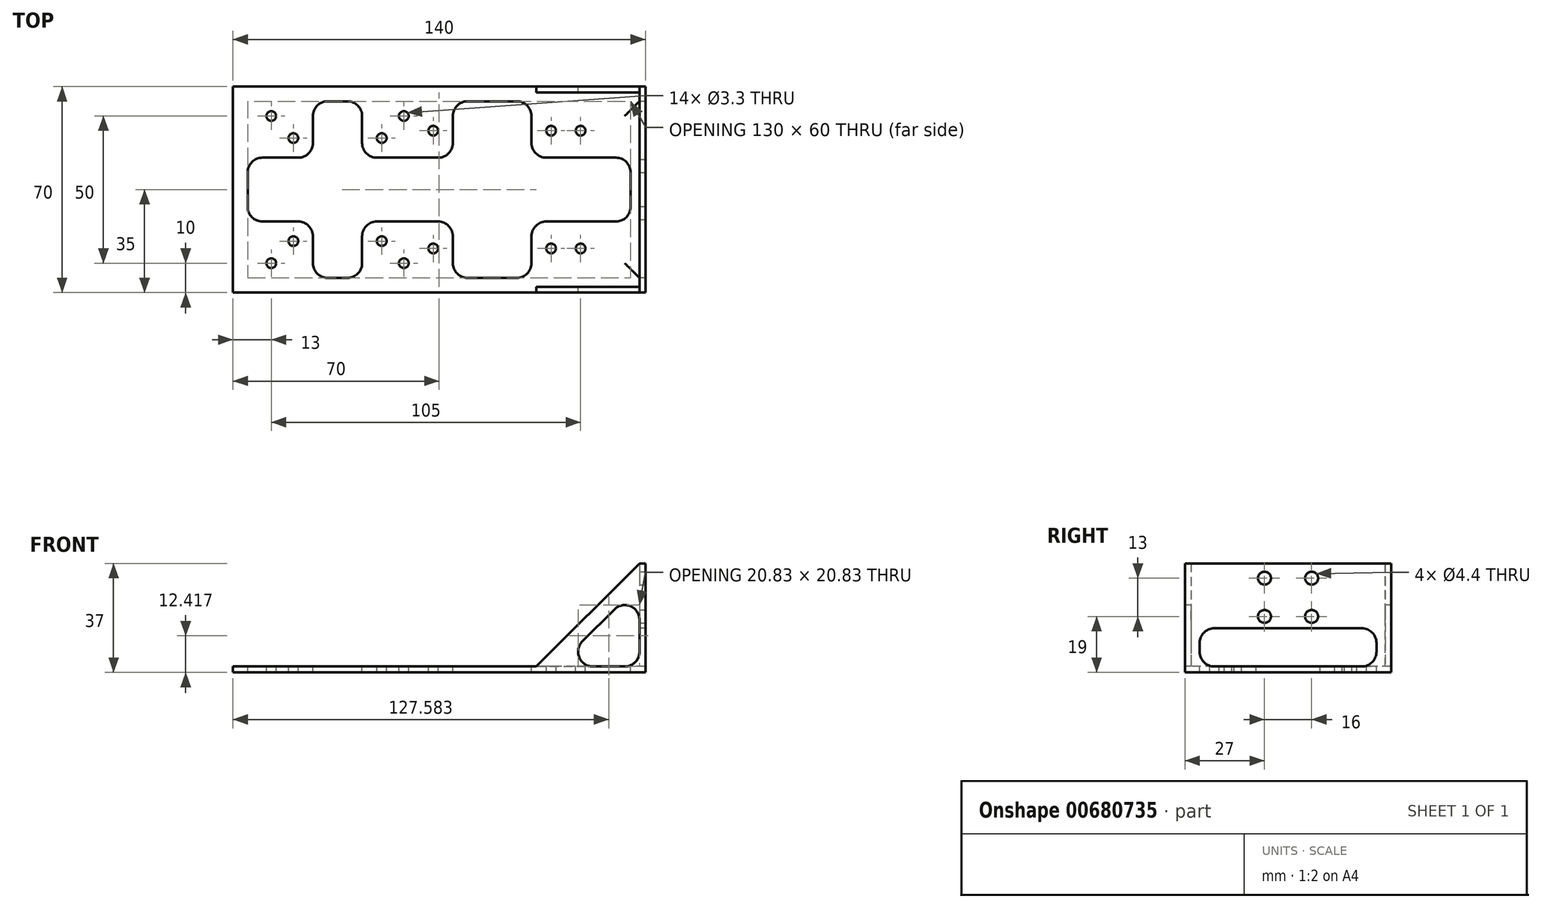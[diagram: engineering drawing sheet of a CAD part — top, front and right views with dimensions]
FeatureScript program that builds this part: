
annotation { "Feature Type Name" : "Feature", "Feature Type Description" : "" }
export const myFeature = defineFeature(function(context is Context, id is Id, definition is map)
    precondition{}
    {
        {
            var Q0;
            Q0=qCreatedBy(makeId("Top.planeOp"),FACE);
            var sketch = newSketch(context, id + "F0", { "sketchPlane" : qUnion([Q0])});
            skLineSegment(sketch, "E0.bottom", {"start": v(-80, 35) * mm, "end": v(60, 35) * mm});
            skLineSegment(sketch, "E0.top", {"start": v(-80, -35) * mm, "end": v(60, -35) * mm});
            skLineSegment(sketch, "E0.left", {"start": v(-80, 35) * mm, "end": v(-80, -35) * mm});
            skLineSegment(sketch, "E0.right", {"start": v(60, 35) * mm, "end": v(60, -35) * mm});
            skSolve(sketch);
        }
        {
            var Q0;
            Q0 = qSketchRegion(id + "F0", true);
            extrude(context, id + "F1", {"entities" : qUnion([Q0]), "depth" : 37 * mm, "offsetDistance" : 25 * mm});
        }
        {
            var Q0;
            Q0=makeQuery(id+"F1.opExtrude","SWEPT_FACE",FACE,{"disambiguationData":[OSD([sQuery(id+"F0.wireOp",EDGE,"E0.top")])]});
            var sketch = newSketch(context, id + "F2", { "sketchPlane" : qUnion([Q0])});
            skLineSegment(sketch, "E1.bottom", {"start": v(-80, 37) * mm, "end": v(58, 37) * mm});
            skLineSegment(sketch, "E1.top", {"start": v(-80, 2) * mm, "end": v(58, 2) * mm});
            skLineSegment(sketch, "E1.left", {"start": v(-80, 37) * mm, "end": v(-80, 2) * mm});
            skLineSegment(sketch, "E2", {"start": v(58, 37) * mm, "end": v(58, 2) * mm});
            skSolve(sketch);
        }
        {
            var Q0;
            Q0=makeQuery(id+"F2.imprint","IMPRINT",FACE,{"disambiguationData":[TD([[makeQuery(id+"F2.imprint","IMPRINT",EDGE,{"derivedFrom":sQuery(id+"F2.wireOp",EDGE,"E1.bottom")}),-1.0]])]});
            var Q1;
            Q1=makeQuery(id+"F2.imprint","IMPRINT",FACE,{"disambiguationData":[TD([[makeQuery(id+"F2.imprint","IMPRINT",EDGE,{"derivedFrom":sQuery(id+"F2.wireOp",EDGE,"E1.right")}),1.0]])]});
            extrude(context, id + "F3", {"entities" : qUnion([Q0, Q1]), "operationType" : NewBodyOperationType.REMOVE, "endBound" : BoundingType.THROUGH_ALL, "oppositeDirection" : true, "depth" : 25 * mm, "offsetDistance" : 25 * mm});
        }
        {
            var Q0;
            Q0=makeQuery(id+"F3.boolean.opBoolean","COPY",FACE,{"derivedFrom":makeQuery(id+"F3.opExtrude","SWEPT_FACE",FACE,{"disambiguationData":[OSD([sQuery(id+"F2.wireOp",EDGE,"E1.top")])]})});
            var sketch = newSketch(context, id + "F4", { "sketchPlane" : qUnion([Q0])});
            skPoint(sketch, "E3", {"position": v(38, -20) * mm});
            skPoint(sketch, "E4", {"position": v(38, 20) * mm});
            skPoint(sketch, "E5", {"position": v(28, 20) * mm});
            skPoint(sketch, "E6", {"position": v(28, -20) * mm});
            skPoint(sketch, "E7", {"position": v(-12, -20) * mm});
            skPoint(sketch, "E8", {"position": v(-12, 20) * mm});
            skPoint(sketch, "E9", {"position": v(-67, 25) * mm});
            skPoint(sketch, "E10", {"position": v(-59.5, -17.5) * mm});
            skPoint(sketch, "E11", {"position": v(-29.5, 17.5) * mm});
            skPoint(sketch, "E12", {"position": v(-29.5, -17.5) * mm});
            skPoint(sketch, "E13", {"position": v(-22, 25) * mm});
            skPoint(sketch, "E14", {"position": v(-67, -25) * mm});
            skPoint(sketch, "E15", {"position": v(-22, -25) * mm});
            skPoint(sketch, "E16", {"position": v(-59.5, 17.5) * mm});
            skSolve(sketch);
        }
        {
            var Q0;
            Q0=sQuery(id+"F4.wireOp",VERTEX,"E9");
            var Q1;
            Q1=sQuery(id+"F4.wireOp",VERTEX,"E16");
            var Q2;
            Q2=sQuery(id+"F4.wireOp",VERTEX,"E14");
            var Q3;
            Q3=sQuery(id+"F4.wireOp",VERTEX,"E10");
            var Q4;
            Q4=sQuery(id+"F4.wireOp",VERTEX,"E12");
            var Q5;
            Q5=sQuery(id+"F4.wireOp",VERTEX,"E15");
            var Q6;
            Q6=sQuery(id+"F4.wireOp",VERTEX,"E7");
            var Q7;
            Q7=sQuery(id+"F4.wireOp",VERTEX,"E8");
            var Q8;
            Q8=sQuery(id+"F4.wireOp",VERTEX,"E13");
            var Q9;
            Q9=sQuery(id+"F4.wireOp",VERTEX,"E11");
            var Q10;
            Q10=sQuery(id+"F4.wireOp",VERTEX,"E5");
            var Q11;
            Q11=sQuery(id+"F4.wireOp",VERTEX,"E4");
            var Q12;
            Q12=sQuery(id+"F4.wireOp",VERTEX,"E3");
            var Q13;
            Q13=sQuery(id+"F4.wireOp",VERTEX,"E6");
            var Q14;
            Q14=makeQuery(id+"F1.opExtrude","SWEPT_BODY",BODY,{"disambiguationData":[OSD([sQuery(id+"F0.wireOp",EDGE,"E0.bottom"),sQuery(id+"F0.wireOp",EDGE,"E0.top"),sQuery(id+"F0.wireOp",EDGE,"E0.left"),sQuery(id+"F0.wireOp",EDGE,"E0.right")])]});
            hole(context, id + "F5", {"style" : HoleStyle.SIMPLE, "endStyle" : HoleEndStyle.THROUGH, "standardTappedOrClearance" : lookupTablePath({ "standard" : "ISO", "fit" : "Normal", "size" : "M3", "type" : "Clearance" }), "standardBlindInLast" : lookupTablePath({ "fit" : "Standard", "standard" : "ISO", "size" : "M3", "type" : "Clearance" }), "holeDiameter" : 3.3 * mm, "majorDiameter" : 5 * mm, "isTappedThrough" : true, "tappedDepth" : 12 * mm, "tapClearance" : 3, "locations" : qUnion([Q0, Q1, Q2, Q3, Q4, Q5, Q6, Q7, Q8, Q9, Q10, Q11, Q12, Q13]), "scope" : qUnion([Q14])});
        }
        {
            var Q0;
            Q0=makeQuery(id+"F3.boolean.opBoolean","COPY",FACE,{"derivedFrom":makeQuery(id+"F3.opExtrude","SWEPT_FACE",FACE,{"disambiguationData":[OSD([sQuery(id+"F2.wireOp",EDGE,"E2")])]})});
            var sketch = newSketch(context, id + "F6", { "sketchPlane" : qUnion([Q0])});
            skLineSegment(sketch, "E17.bottom", {"start": v(-35, 37) * mm, "end": v(-33, 37) * mm});
            skLineSegment(sketch, "E17.top", {"start": v(-35, 2) * mm, "end": v(-33, 2) * mm});
            skLineSegment(sketch, "E17.left", {"start": v(-35, 37) * mm, "end": v(-35, 2) * mm});
            skLineSegment(sketch, "E17.right", {"start": v(-33, 37) * mm, "end": v(-33, 2) * mm});
            skLineSegment(sketch, "E18.bottom", {"start": v(35, 37) * mm, "end": v(33, 37) * mm});
            skLineSegment(sketch, "E18.top", {"start": v(35, 2) * mm, "end": v(33, 2) * mm});
            skLineSegment(sketch, "E18.left", {"start": v(35, 37) * mm, "end": v(35, 2) * mm});
            skLineSegment(sketch, "E18.right", {"start": v(33, 37) * mm, "end": v(33, 2) * mm});
            skSolve(sketch);
        }
        {
            var Q0;
            Q0 = qSketchRegion(id + "F6", true);
            extrude(context, id + "F7", {"entities" : qUnion([Q0]), "operationType" : NewBodyOperationType.ADD, "depth" : 35 * mm, "offsetDistance" : 25 * mm});
        }
        {
            var Q0;
            Q0=makeQuery(id+"F7.opExtrude","CAP_EDGE",EDGE,{"disambiguationData":[OSD([sQuery(id+"F6.wireOp",EDGE,"E18.bottom")])],"isStart":false});
            var Q1;
            Q1=makeQuery(id+"F7.opExtrude","CAP_EDGE",EDGE,{"disambiguationData":[OSD([sQuery(id+"F6.wireOp",EDGE,"E17.bottom")])],"isStart":false});
            chamfer(context, id + "F8", {"entities" : qUnion([Q0, Q1]), "width" : 35 * mm, "tangentPropagation" : true});
        }
        {
            var Q0;
            Q0=makeQuery(id+"F7.boolean.opBoolean","MERGE",FACE,{"derivedFrom":[makeQuery(id+"F1.opExtrude","SWEPT_FACE",FACE,{"disambiguationData":[OSD([sQuery(id+"F0.wireOp",EDGE,"E0.top")])]}),makeQuery(id+"F7.opExtrude","SWEPT_FACE",FACE,{"disambiguationData":[OSD([sQuery(id+"F6.wireOp",EDGE,"E18.left")])]})]});
            var sketch = newSketch(context, id + "F9", { "sketchPlane" : qUnion([Q0])});
            skLineSegment(sketch, "E19", {"start": v(58, 29.93) * mm, "end": v(30.07, 2) * mm});
            skLineSegment(sketch, "E20", {"start": v(30.07, 2) * mm, "end": v(58, 2) * mm});
            skLineSegment(sketch, "E21", {"start": v(58, 2) * mm, "end": v(58, 29.93) * mm});
            skSolve(sketch);
        }
        {
            var Q0;
            Q0 = qSketchRegion(id + "F9", true);
            extrude(context, id + "F10", {"entities" : qUnion([Q0]), "operationType" : NewBodyOperationType.REMOVE, "endBound" : BoundingType.THROUGH_ALL, "oppositeDirection" : true, "depth" : 25 * mm, "offsetDistance" : 25 * mm});
        }
        {
            var Q0;
            Q0=makeQuery(id+"F10.boolean.opBoolean","MERGE",FACE,{"derivedFrom":[makeQuery(id+"F3.boolean.opBoolean","COPY",FACE,{"derivedFrom":makeQuery(id+"F3.opExtrude","SWEPT_FACE",FACE,{"disambiguationData":[OSD([sQuery(id+"F2.wireOp",EDGE,"E2")])]})}),makeQuery(id+"F10.opExtrude","SWEPT_FACE",FACE,{"disambiguationData":[OSD([sQuery(id+"F9.wireOp",EDGE,"E21")])]})]});
            var sketch = newSketch(context, id + "F11", { "sketchPlane" : qUnion([Q0])});
            skLineSegment(sketch, "E22.bottom", {"start": v(-30, 15) * mm, "end": v(30, 15) * mm});
            skLineSegment(sketch, "E22.top", {"start": v(-30, 2) * mm, "end": v(30, 2) * mm});
            skLineSegment(sketch, "E22.left", {"start": v(-30, 15) * mm, "end": v(-30, 2) * mm});
            skLineSegment(sketch, "E22.right", {"start": v(30, 15) * mm, "end": v(30, 2) * mm});
            skSolve(sketch);
        }
        {
            var Q0;
            Q0 = qSketchRegion(id + "F11", true);
            extrude(context, id + "F12", {"entities" : qUnion([Q0]), "operationType" : NewBodyOperationType.REMOVE, "endBound" : BoundingType.THROUGH_ALL, "oppositeDirection" : true, "depth" : 25 * mm, "offsetDistance" : 25 * mm});
        }
        {
            var Q0;
            Q0=makeQuery(id+"F12.boolean.opBoolean","MERGE",FACE,{"derivedFrom":[makeQuery(id+"F10.boolean.opBoolean","MERGE",FACE,{"derivedFrom":[makeQuery(id+"F3.boolean.opBoolean","COPY",FACE,{"derivedFrom":makeQuery(id+"F3.opExtrude","SWEPT_FACE",FACE,{"disambiguationData":[OSD([sQuery(id+"F2.wireOp",EDGE,"E1.top")])]})}),makeQuery(id+"F10.opExtrude","SWEPT_FACE",FACE,{"disambiguationData":[OSD([sQuery(id+"F9.wireOp",EDGE,"E20")])]})]}),makeQuery(id+"F12.opExtrude","SWEPT_FACE",FACE,{"disambiguationData":[OSD([sQuery(id+"F11.wireOp",EDGE,"E22.top")])]})]});
            var sketch = newSketch(context, id + "F13", { "sketchPlane" : qUnion([Q0])});
            skLineSegment(sketch, "E23.bottom", {"start": v(55, 10.85) * mm, "end": v(-75, 10.85) * mm});
            skLineSegment(sketch, "E23.top", {"start": v(55, -10.85) * mm, "end": v(-75, -10.85) * mm});
            skLineSegment(sketch, "E23.left", {"start": v(55, 10.85) * mm, "end": v(55, -10.85) * mm});
            skLineSegment(sketch, "E23.right", {"start": v(-75, 10.85) * mm, "end": v(-75, -10.85) * mm});
            skLineSegment(sketch, "E24.bottom", {"start": v(21.35, 30) * mm, "end": v(-5.35, 30) * mm});
            skLineSegment(sketch, "E24.top", {"start": v(21.35, -30) * mm, "end": v(-5.35, -30) * mm});
            skLineSegment(sketch, "E24.left", {"start": v(21.35, 30) * mm, "end": v(21.35, -30) * mm});
            skLineSegment(sketch, "E24.right", {"start": v(-5.35, 30) * mm, "end": v(-5.35, -30) * mm});
            skLineSegment(sketch, "E25.bottom", {"start": v(-36.15, 30) * mm, "end": v(-52.85, 30) * mm});
            skLineSegment(sketch, "E25.top", {"start": v(-36.15, -30) * mm, "end": v(-52.85, -30) * mm});
            skLineSegment(sketch, "E25.left", {"start": v(-36.15, 30) * mm, "end": v(-36.15, -30) * mm});
            skLineSegment(sketch, "E25.right", {"start": v(-52.85, 30) * mm, "end": v(-52.85, -30) * mm});
            skSolve(sketch);
        }
        {
            var Q0;
            Q0 = qSketchRegion(id + "F13", true);
            extrude(context, id + "F14", {"entities" : qUnion([Q0]), "operationType" : NewBodyOperationType.REMOVE, "endBound" : BoundingType.THROUGH_ALL, "oppositeDirection" : true, "depth" : 25 * mm, "offsetDistance" : 25 * mm});
        }
        {
            var Q0;
            Q0=makeQuery(id+"F14.boolean.opBoolean","COPY",EDGE,{"derivedFrom":makeQuery(id+"F14.opExtrude","SWEPT_EDGE",EDGE,{"disambiguationData":[OSD([sQuery(id+"F13.wireOp",EDGE,"E23.bottom"),sQuery(id+"F13.wireOp",EDGE,"E23.left")])]})});
            var Q1;
            Q1=makeQuery(id+"F14.boolean.opBoolean","COPY",EDGE,{"derivedFrom":makeQuery(id+"F14.opExtrude","SWEPT_EDGE",EDGE,{"disambiguationData":[OSD([sQuery(id+"F13.wireOp",EDGE,"E23.top"),sQuery(id+"F13.wireOp",EDGE,"E23.left")])]})});
            var Q2;
            Q2=makeQuery(id+"F14.boolean.opBoolean","COPY",EDGE,{"derivedFrom":makeQuery(id+"F14.opExtrude","SWEPT_EDGE",EDGE,{"disambiguationData":[OSD([sQuery(id+"F13.wireOp",EDGE,"E23.top"),sQuery(id+"F13.wireOp",EDGE,"E24.left")])]})});
            var Q3;
            Q3=makeQuery(id+"F14.boolean.opBoolean","COPY",EDGE,{"derivedFrom":makeQuery(id+"F14.opExtrude","SWEPT_EDGE",EDGE,{"disambiguationData":[OSD([sQuery(id+"F13.wireOp",EDGE,"E23.bottom"),sQuery(id+"F13.wireOp",EDGE,"E24.left")])]})});
            var Q4;
            Q4=makeQuery(id+"F14.boolean.opBoolean","COPY",EDGE,{"derivedFrom":makeQuery(id+"F14.opExtrude","SWEPT_EDGE",EDGE,{"disambiguationData":[OSD([sQuery(id+"F13.wireOp",EDGE,"E24.top"),sQuery(id+"F13.wireOp",EDGE,"E24.left")])]})});
            var Q5;
            Q5=makeQuery(id+"F14.boolean.opBoolean","COPY",EDGE,{"derivedFrom":makeQuery(id+"F14.opExtrude","SWEPT_EDGE",EDGE,{"disambiguationData":[OSD([sQuery(id+"F13.wireOp",EDGE,"E24.bottom"),sQuery(id+"F13.wireOp",EDGE,"E24.left")])]})});
            var Q6;
            Q6=makeQuery(id+"F14.boolean.opBoolean","COPY",EDGE,{"derivedFrom":makeQuery(id+"F14.opExtrude","SWEPT_EDGE",EDGE,{"disambiguationData":[OSD([sQuery(id+"F13.wireOp",EDGE,"E24.top"),sQuery(id+"F13.wireOp",EDGE,"E24.right")])]})});
            var Q7;
            Q7=makeQuery(id+"F14.boolean.opBoolean","COPY",EDGE,{"derivedFrom":makeQuery(id+"F14.opExtrude","SWEPT_EDGE",EDGE,{"disambiguationData":[OSD([sQuery(id+"F13.wireOp",EDGE,"E23.top"),sQuery(id+"F13.wireOp",EDGE,"E24.right")])]})});
            var Q8;
            Q8=makeQuery(id+"F14.boolean.opBoolean","COPY",EDGE,{"derivedFrom":makeQuery(id+"F14.opExtrude","SWEPT_EDGE",EDGE,{"disambiguationData":[OSD([sQuery(id+"F13.wireOp",EDGE,"E23.bottom"),sQuery(id+"F13.wireOp",EDGE,"E24.right")])]})});
            var Q9;
            Q9=makeQuery(id+"F14.boolean.opBoolean","COPY",EDGE,{"derivedFrom":makeQuery(id+"F14.opExtrude","SWEPT_EDGE",EDGE,{"disambiguationData":[OSD([sQuery(id+"F13.wireOp",EDGE,"E24.bottom"),sQuery(id+"F13.wireOp",EDGE,"E24.right")])]})});
            var Q10;
            Q10=makeQuery(id+"F14.boolean.opBoolean","COPY",EDGE,{"derivedFrom":makeQuery(id+"F14.opExtrude","SWEPT_EDGE",EDGE,{"disambiguationData":[OSD([sQuery(id+"F13.wireOp",EDGE,"E23.bottom"),sQuery(id+"F13.wireOp",EDGE,"E25.left")])]})});
            var Q11;
            Q11=makeQuery(id+"F14.boolean.opBoolean","COPY",EDGE,{"derivedFrom":makeQuery(id+"F14.opExtrude","SWEPT_EDGE",EDGE,{"disambiguationData":[OSD([sQuery(id+"F13.wireOp",EDGE,"E25.top"),sQuery(id+"F13.wireOp",EDGE,"E25.left")])]})});
            var Q12;
            Q12=makeQuery(id+"F14.boolean.opBoolean","COPY",EDGE,{"derivedFrom":makeQuery(id+"F14.opExtrude","SWEPT_EDGE",EDGE,{"disambiguationData":[OSD([sQuery(id+"F13.wireOp",EDGE,"E23.top"),sQuery(id+"F13.wireOp",EDGE,"E25.left")])]})});
            var Q13;
            Q13=makeQuery(id+"F14.boolean.opBoolean","COPY",EDGE,{"derivedFrom":makeQuery(id+"F14.opExtrude","SWEPT_EDGE",EDGE,{"disambiguationData":[OSD([sQuery(id+"F13.wireOp",EDGE,"E25.bottom"),sQuery(id+"F13.wireOp",EDGE,"E25.left")])]})});
            var Q14;
            Q14=makeQuery(id+"F14.boolean.opBoolean","COPY",EDGE,{"derivedFrom":makeQuery(id+"F14.opExtrude","SWEPT_EDGE",EDGE,{"disambiguationData":[OSD([sQuery(id+"F13.wireOp",EDGE,"E25.top"),sQuery(id+"F13.wireOp",EDGE,"E25.right")])]})});
            var Q15;
            Q15=makeQuery(id+"F14.boolean.opBoolean","COPY",EDGE,{"derivedFrom":makeQuery(id+"F14.opExtrude","SWEPT_EDGE",EDGE,{"disambiguationData":[OSD([sQuery(id+"F13.wireOp",EDGE,"E23.top"),sQuery(id+"F13.wireOp",EDGE,"E25.right")])]})});
            var Q16;
            Q16=makeQuery(id+"F14.boolean.opBoolean","COPY",EDGE,{"derivedFrom":makeQuery(id+"F14.opExtrude","SWEPT_EDGE",EDGE,{"disambiguationData":[OSD([sQuery(id+"F13.wireOp",EDGE,"E23.top"),sQuery(id+"F13.wireOp",EDGE,"E23.right")])]})});
            var Q17;
            Q17=makeQuery(id+"F14.boolean.opBoolean","COPY",EDGE,{"derivedFrom":makeQuery(id+"F14.opExtrude","SWEPT_EDGE",EDGE,{"disambiguationData":[OSD([sQuery(id+"F13.wireOp",EDGE,"E23.bottom"),sQuery(id+"F13.wireOp",EDGE,"E25.right")])]})});
            var Q18;
            Q18=makeQuery(id+"F14.boolean.opBoolean","COPY",EDGE,{"derivedFrom":makeQuery(id+"F14.opExtrude","SWEPT_EDGE",EDGE,{"disambiguationData":[OSD([sQuery(id+"F13.wireOp",EDGE,"E23.bottom"),sQuery(id+"F13.wireOp",EDGE,"E23.right")])]})});
            var Q19;
            Q19=makeQuery(id+"F14.boolean.opBoolean","COPY",EDGE,{"derivedFrom":makeQuery(id+"F14.opExtrude","SWEPT_EDGE",EDGE,{"disambiguationData":[OSD([sQuery(id+"F13.wireOp",EDGE,"E25.bottom"),sQuery(id+"F13.wireOp",EDGE,"E25.right")])]})});
            var Q20;
            {var subQ0=sQuery(id+"F9.wireOp",EDGE,"E19");var subQ1=sQuery(id+"F9.wireOp",EDGE,"E20");Q20=makeQuery(id+"F10.boolean.opBoolean","COPY",EDGE,{"disambiguationData":[TD([makeQuery(id+"F1.opExtrude","SWEPT_FACE",FACE,{"disambiguationData":[OSD([sQuery(id+"F0.wireOp",EDGE,"E0.top")])]})])],"derivedFrom":makeQuery(id+"F10.opExtrude","SWEPT_EDGE",EDGE,{"disambiguationData":[OSD([subQ0,subQ1])]})});}
            var Q21;
            {var subQ0=sQuery(id+"F9.wireOp",EDGE,"E19");var subQ1=sQuery(id+"F9.wireOp",EDGE,"E20");Q21=makeQuery(id+"F10.boolean.opBoolean","COPY",EDGE,{"disambiguationData":[TD([makeQuery(id+"F1.opExtrude","SWEPT_FACE",FACE,{"disambiguationData":[OSD([sQuery(id+"F0.wireOp",EDGE,"E0.bottom")])]})])],"derivedFrom":makeQuery(id+"F10.opExtrude","SWEPT_EDGE",EDGE,{"disambiguationData":[OSD([subQ0,subQ1])]})});}
            var Q22;
            {var subQ0=sQuery(id+"F2.wireOp",EDGE,"E2");var subQ1=sQuery(id+"F2.wireOp",EDGE,"E1.top");var subQ2=sQuery(id+"F9.wireOp",EDGE,"E20");var subQ3=sQuery(id+"F9.wireOp",EDGE,"E21");Q22=makeQuery(id+"F12.boolean.opBoolean","SPLIT",EDGE,{"disambiguationData":[TD([makeQuery(id+"F1.opExtrude","SWEPT_FACE",FACE,{"disambiguationData":[OSD([sQuery(id+"F0.wireOp",EDGE,"E0.bottom")])]})])],"derivedFrom":makeQuery(id+"F10.boolean.opBoolean","MERGE",EDGE,{"derivedFrom":[makeQuery(id+"F3.boolean.opBoolean","COPY",EDGE,{"derivedFrom":makeQuery(id+"F3.opExtrude","SWEPT_EDGE",EDGE,{"disambiguationData":[OSD([subQ1,subQ0])]})}),makeQuery(id+"F10.opExtrude","SWEPT_EDGE",EDGE,{"disambiguationData":[OSD([subQ2,subQ3])]})]})});}
            var Q23;
            {var subQ0=sQuery(id+"F9.wireOp",EDGE,"E19");var subQ1=sQuery(id+"F9.wireOp",EDGE,"E21");Q23=makeQuery(id+"F10.boolean.opBoolean","COPY",EDGE,{"disambiguationData":[TD([makeQuery(id+"F1.opExtrude","SWEPT_FACE",FACE,{"disambiguationData":[OSD([sQuery(id+"F0.wireOp",EDGE,"E0.bottom")])]})])],"derivedFrom":makeQuery(id+"F10.opExtrude","SWEPT_EDGE",EDGE,{"disambiguationData":[OSD([subQ0,subQ1])]})});}
            var Q24;
            {var subQ0=sQuery(id+"F2.wireOp",EDGE,"E2");var subQ1=sQuery(id+"F2.wireOp",EDGE,"E1.top");var subQ2=sQuery(id+"F9.wireOp",EDGE,"E21");var subQ3=sQuery(id+"F9.wireOp",EDGE,"E20");Q24=makeQuery(id+"F12.boolean.opBoolean","SPLIT",EDGE,{"disambiguationData":[TD([makeQuery(id+"F1.opExtrude","SWEPT_FACE",FACE,{"disambiguationData":[OSD([sQuery(id+"F0.wireOp",EDGE,"E0.top")])]})])],"derivedFrom":makeQuery(id+"F10.boolean.opBoolean","MERGE",EDGE,{"derivedFrom":[makeQuery(id+"F3.boolean.opBoolean","COPY",EDGE,{"derivedFrom":makeQuery(id+"F3.opExtrude","SWEPT_EDGE",EDGE,{"disambiguationData":[OSD([subQ1,subQ0])]})}),makeQuery(id+"F10.opExtrude","SWEPT_EDGE",EDGE,{"disambiguationData":[OSD([subQ3,subQ2])]})]})});}
            var Q25;
            {var subQ0=sQuery(id+"F9.wireOp",EDGE,"E19");var subQ1=sQuery(id+"F9.wireOp",EDGE,"E21");Q25=makeQuery(id+"F10.boolean.opBoolean","COPY",EDGE,{"disambiguationData":[TD([makeQuery(id+"F1.opExtrude","SWEPT_FACE",FACE,{"disambiguationData":[OSD([sQuery(id+"F0.wireOp",EDGE,"E0.top")])]})])],"derivedFrom":makeQuery(id+"F10.opExtrude","SWEPT_EDGE",EDGE,{"disambiguationData":[OSD([subQ0,subQ1])]})});}
            var Q26;
            Q26=makeQuery(id+"F12.boolean.opBoolean","COPY",EDGE,{"derivedFrom":makeQuery(id+"F12.opExtrude","SWEPT_EDGE",EDGE,{"disambiguationData":[OSD([sQuery(id+"F2.wireOp",EDGE,"E1.top"),sQuery(id+"F2.wireOp",EDGE,"E2"),sQuery(id+"F9.wireOp",EDGE,"E20"),sQuery(id+"F9.wireOp",EDGE,"E21"),sQuery(id+"F11.wireOp",EDGE,"E22.top"),sQuery(id+"F11.wireOp",EDGE,"E22.right")])]})});
            var Q27;
            Q27=makeQuery(id+"F12.boolean.opBoolean","COPY",EDGE,{"derivedFrom":makeQuery(id+"F12.opExtrude","SWEPT_EDGE",EDGE,{"disambiguationData":[OSD([sQuery(id+"F2.wireOp",EDGE,"E1.top"),sQuery(id+"F2.wireOp",EDGE,"E2"),sQuery(id+"F9.wireOp",EDGE,"E20"),sQuery(id+"F9.wireOp",EDGE,"E21"),sQuery(id+"F11.wireOp",EDGE,"E22.top"),sQuery(id+"F11.wireOp",EDGE,"E22.left")])]})});
            var Q28;
            Q28=makeQuery(id+"F12.boolean.opBoolean","COPY",EDGE,{"derivedFrom":makeQuery(id+"F12.opExtrude","SWEPT_EDGE",EDGE,{"disambiguationData":[OSD([sQuery(id+"F11.wireOp",EDGE,"E22.bottom"),sQuery(id+"F11.wireOp",EDGE,"E22.right")])]})});
            var Q29;
            Q29=makeQuery(id+"F12.boolean.opBoolean","COPY",EDGE,{"derivedFrom":makeQuery(id+"F12.opExtrude","SWEPT_EDGE",EDGE,{"disambiguationData":[OSD([sQuery(id+"F11.wireOp",EDGE,"E22.bottom"),sQuery(id+"F11.wireOp",EDGE,"E22.left")])]})});
            fillet(context, id + "F15", {"entities" : qUnion([Q0, Q1, Q2, Q3, Q4, Q5, Q6, Q7, Q8, Q9, Q10, Q11, Q12, Q13, Q14, Q15, Q16, Q17, Q18, Q19, Q20, Q21, Q22, Q23, Q24, Q25, Q26, Q27, Q28, Q29]), "radius" : 5 * mm, "tangentPropagation" : true, "allowEdgeOverflow" : false});
        }
        {
            var Q0;
            Q0=makeQuery(id+"F1.opExtrude","SWEPT_FACE",FACE,{"disambiguationData":[OSD([sQuery(id+"F0.wireOp",EDGE,"E0.right")])]});
            var sketch = newSketch(context, id + "F16", { "sketchPlane" : qUnion([Q0])});
            skPoint(sketch, "E26", {"position": v(8, 32) * mm});
            skPoint(sketch, "E27", {"position": v(-8, 32) * mm});
            skPoint(sketch, "E28", {"position": v(-8, 19) * mm});
            skPoint(sketch, "E29", {"position": v(8, 19) * mm});
            skSolve(sketch);
        }
        {
            var Q0;
            Q0=sQuery(id+"F16.wireOp",VERTEX,"E27");
            var Q1;
            Q1=sQuery(id+"F16.wireOp",VERTEX,"E26");
            var Q2;
            Q2=sQuery(id+"F16.wireOp",VERTEX,"E28");
            var Q3;
            Q3=sQuery(id+"F16.wireOp",VERTEX,"E29");
            var Q4;
            Q4=makeQuery(id+"F1.opExtrude","SWEPT_BODY",BODY,{"disambiguationData":[OSD([sQuery(id+"F0.wireOp",EDGE,"E0.bottom"),sQuery(id+"F0.wireOp",EDGE,"E0.top"),sQuery(id+"F0.wireOp",EDGE,"E0.left"),sQuery(id+"F0.wireOp",EDGE,"E0.right")])]});
            hole(context, id + "F17", {"style" : HoleStyle.SIMPLE, "endStyle" : HoleEndStyle.THROUGH, "standardTappedOrClearance" : lookupTablePath({ "standard" : "ISO", "fit" : "Normal", "size" : "M4", "type" : "Clearance" }), "standardBlindInLast" : lookupTablePath({ "fit" : "Standard", "standard" : "ISO", "size" : "M4", "type" : "Clearance" }), "holeDiameter" : 4.4 * mm, "majorDiameter" : 5 * mm, "isTappedThrough" : true, "tappedDepth" : 12 * mm, "tapClearance" : 3, "locations" : qUnion([Q0, Q1, Q2, Q3]), "scope" : qUnion([Q4])});
        }
    });
